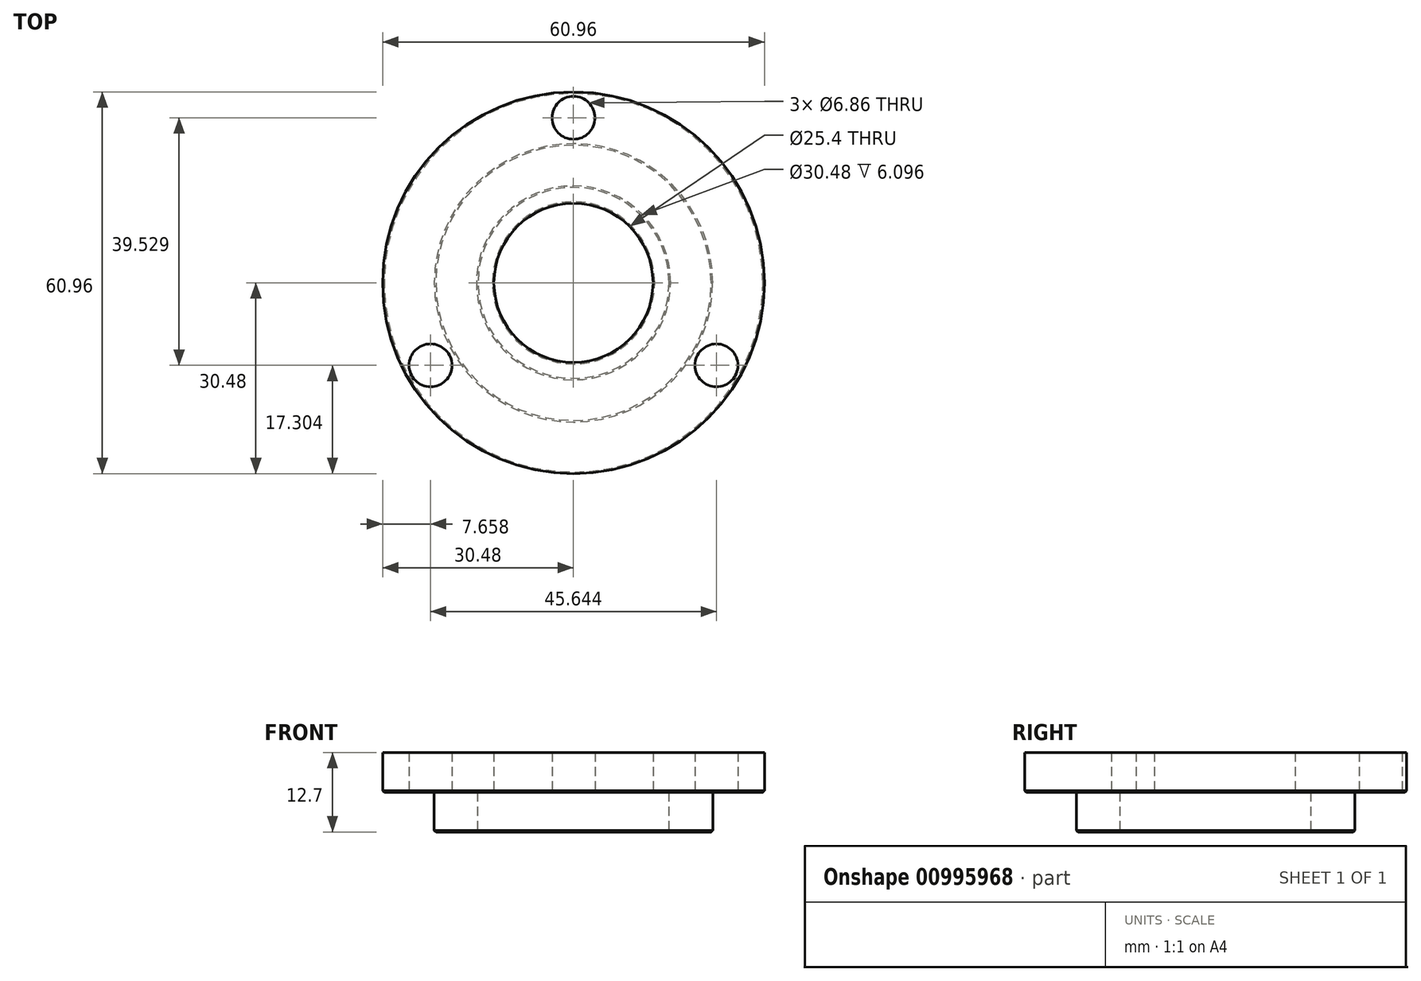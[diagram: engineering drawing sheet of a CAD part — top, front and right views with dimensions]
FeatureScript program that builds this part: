
annotation { "Feature Type Name" : "Feature", "Feature Type Description" : "" }
export const myFeature = defineFeature(function(context is Context, id is Id, definition is map)
    precondition{}
    {
        {
            var Q0;
            Q0=qCreatedBy(makeId("Top.planeOp"),FACE);
            var sketch = newSketch(context, id + "F0", { "sketchPlane" : qUnion([Q0])});
            skCircle(sketch, "E0", {"center": v(0, 0) * mm, "radius": 30.48 * mm});
            skCircle(sketch, "E1", {"center": v(0, 0) * mm, "radius": 12.7 * mm});
            skSolve(sketch);
        }
        {
            var Q0;
            Q0=makeQuery(id+"F0.imprint","IMPRINT",FACE,{"disambiguationData":[TD([[makeQuery(id+"F0.imprint","IMPRINT",EDGE,{"derivedFrom":sQuery(id+"F0.wireOp",EDGE,"E0")}),1.0]])]});
            extrude(context, id + "F1", {"entities" : qUnion([Q0]), "depth" : 6.35 * mm, "offsetDistance" : 25.4 * mm});
        }
        {
            var Q0;
            Q0=qCreatedBy(makeId("Top.planeOp"),FACE);
            var sketch = newSketch(context, id + "F2", { "sketchPlane" : qUnion([Q0])});
            skCircle(sketch, "E2", {"center": v(0, 0) * mm, "radius": 22.23 * mm});
            skCircle(sketch, "E3", {"center": v(0, 0) * mm, "radius": 26.35 * mm, "construction": true});
            skLineSegment(sketch, "E4", {"start": v(0, 0) * mm, "end": v(0, 34.3) * mm, "construction": true});
            skCircle(sketch, "E5", {"center": v(0, 26.35) * mm, "radius": 3.43 * mm});
            skCircle(sketch, "E6.1.0", {"center": v(22.82, -13.18) * mm, "radius": 3.43 * mm});
            skCircle(sketch, "E6.2.0", {"center": v(-22.82, -13.18) * mm, "radius": 3.43 * mm});
            skLineSegment(sketch, "E6.anchor1", {"start": v(0, 0) * mm, "end": v(0, 26.35) * mm, "construction": true});
            skLineSegment(sketch, "E6.anchor2", {"start": v(0, 0) * mm, "end": v(-22.82, -13.18) * mm, "construction": true});
            skCircle(sketch, "E7", {"center": v(0, 0) * mm, "radius": 15.24 * mm});
            skSolve(sketch);
        }
        {
            var Q0;
            Q0=makeQuery(id+"F2.imprint","IMPRINT",FACE,{"disambiguationData":[TD([[makeQuery(id+"F2.imprint","IMPRINT",EDGE,{"derivedFrom":sQuery(id+"F2.wireOp",EDGE,"E2")}),1.0]])]});
            extrude(context, id + "F3", {"entities" : qUnion([Q0]), "operationType" : NewBodyOperationType.ADD, "oppositeDirection" : true, "depth" : 6.35 * mm, "offsetDistance" : 25.4 * mm});
        }
        {
            var Q0;
            Q0=makeQuery(id+"F2.imprint","IMPRINT",FACE,{"disambiguationData":[TD([[makeQuery(id+"F2.imprint","IMPRINT",EDGE,{"derivedFrom":sQuery(id+"F2.wireOp",EDGE,"E6.2.0")}),1.0]])]});
            var Q1;
            Q1=makeQuery(id+"F2.imprint","IMPRINT",FACE,{"disambiguationData":[TD([[makeQuery(id+"F2.imprint","IMPRINT",EDGE,{"derivedFrom":sQuery(id+"F2.wireOp",EDGE,"E5")}),1.0]])]});
            var Q2;
            Q2=makeQuery(id+"F2.imprint","IMPRINT",FACE,{"disambiguationData":[TD([[makeQuery(id+"F2.imprint","IMPRINT",EDGE,{"derivedFrom":sQuery(id+"F2.wireOp",EDGE,"E6.1.0")}),1.0]])]});
            extrude(context, id + "F4", {"entities" : qUnion([Q0, Q1, Q2]), "operationType" : NewBodyOperationType.REMOVE, "depth" : 34.8 * mm, "offsetDistance" : 25.4 * mm});
        }
        {
            var Q0;
            Q0=makeQuery(id+"F1.opExtrude","CAP_EDGE",EDGE,{"disambiguationData":[OSD([sQuery(id+"F0.wireOp",EDGE,"E0")])],"isStart":true});
            var Q1;
            Q1=makeQuery(id+"F3.opExtrude","CAP_EDGE",EDGE,{"disambiguationData":[OSD([sQuery(id+"F2.wireOp",EDGE,"E2")])],"isStart":false});
            var Q2;
            Q2=makeQuery(id+"F3.opExtrude","CAP_FACE",FACE,{"disambiguationData":[OSD([sQuery(id+"F2.wireOp",EDGE,"E2"),sQuery(id+"F2.wireOp",EDGE,"E7")])],"isStart":false});
            var Q3;
            Q3=makeQuery(id+"F1.opExtrude","CAP_EDGE",EDGE,{"disambiguationData":[OSD([sQuery(id+"F0.wireOp",EDGE,"E1")])],"isStart":true});
            chamfer(context, id + "F5", {"entities" : qUnion([Q0, Q1, Q2, Q3]), "width" : 0.25 * mm, "tangentPropagation" : true});
        }
    });
